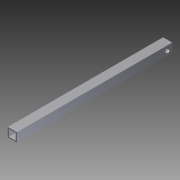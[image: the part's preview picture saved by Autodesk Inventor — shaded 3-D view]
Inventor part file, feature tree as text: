
AUTODESK INVENTOR PART (.ipt)
format: ipt  version: 2012 (Build 160160000, 160)  size: 86,528 bytes
history: native  units: in
note: dims shown in document units (in); Inventor stores cm internally (conversion verified against a paired STEP export)
features: extrude x2, sketch x2
ambient origin geometry x8: Origin, YZ Plane, XZ Plane, XY Plane, X Axis, Y Axis, Z Axis, Center Point
bodies: Solid1 (feature_tree)
feature tree (4):
  extrude  "Extrusion1"  Depth=1.0in
  extrude  "Extrusion2"  Depth=0.125in
  sketch  "Sketch1"  dims[d0=1.0in d1=1.0in]
  sketch  "Sketch2"  dims[d2=0.125in d3=0.125in d4=0.125in d5=0.125in d6=17.0in d7=0.0in d8=0.5in d9=0.5in d10=0.5in d11=17.0in d12=0.0in]
